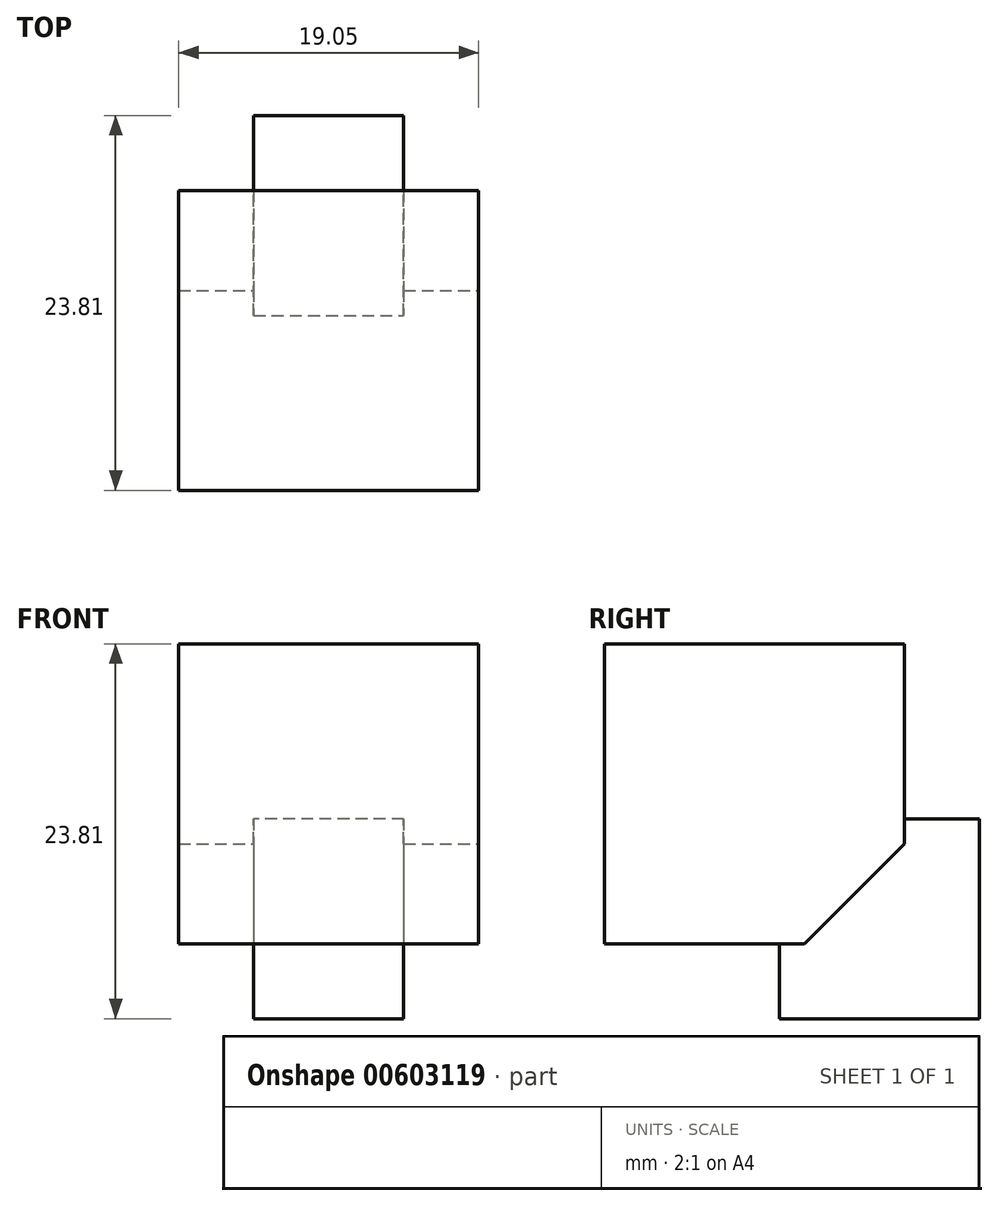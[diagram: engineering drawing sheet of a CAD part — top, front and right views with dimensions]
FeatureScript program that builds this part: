
annotation { "Feature Type Name" : "Feature", "Feature Type Description" : "" }
export const myFeature = defineFeature(function(context is Context, id is Id, definition is map)
    precondition{}
    {
        {
            var Q0;
            Q0=qCreatedBy(makeId("Front.planeOp"),FACE);
            var sketch = newSketch(context, id + "F0", { "sketchPlane" : qUnion([Q0])});
            skLineSegment(sketch, "E0.bottom", {"start": v(0, 0) * mm, "end": v(19.05, 0) * mm});
            skLineSegment(sketch, "E0.top", {"start": v(0, 19.05) * mm, "end": v(19.05, 19.05) * mm});
            skLineSegment(sketch, "E0.left", {"start": v(0, 0) * mm, "end": v(0, 19.05) * mm});
            skLineSegment(sketch, "E0.right", {"start": v(19.05, 0) * mm, "end": v(19.05, 19.05) * mm});
            skSolve(sketch);
        }
        {
            var Q0;
            Q0=qSketchRegion(id+"F0",true);
            extrude(context, id + "F1", {"entities" : qUnion([Q0]), "oppositeDirection" : true, "depth" : 19.05 * mm});
        }
        {
            var Q0;
            Q0=makeQuery(id+"F1.opExtrude","SWEPT_FACE",FACE,{"disambiguationData":[OSD([sQuery(id+"F0.wireOp",EDGE,"E0.right")])]});
            cPlane(context, id + "F2", {"entities" : qUnion([Q0]), "cplaneType" : CPlaneType.OFFSET, "offset" : 9.52 * mm, "oppositeDirection" : true, "width" : 152.4 * mm, "height" : 152.4 * mm});
        }
        {
            var Q0;
            Q0=makeQuery(id+"F1.opExtrude","SWEPT_FACE",FACE,{"disambiguationData":[OSD([sQuery(id+"F0.wireOp",EDGE,"E0.right")])]});
            var sketch = newSketch(context, id + "F3", { "sketchPlane" : qUnion([Q0])});
            skLineSegment(sketch, "E1", {"start": v(12.7, 0) * mm, "end": v(19.05, 6.35) * mm});
            skLineSegment(sketch, "E2", {"start": v(19.05, 0) * mm, "end": v(12.7, 0) * mm});
            skSolve(sketch);
        }
        {
            var Q0;
            Q0=qSketchRegion(id+"F3",true);
            var Q1;
            {var subQ0=sQuery(id+"F3.wireOp",EDGE,"E1");Q1=makeQuery(id+"F3.imprint","IMPRINT",FACE,{"disambiguationData":[TD([[makeQuery(id+"F3.imprint","IMPRINT",EDGE,{"derivedFrom":subQ0}),-1.0]])]});}
            extrude(context, id + "F4", {"entities" : qUnion([Q0, Q1]), "operationType" : NewBodyOperationType.REMOVE, "oppositeDirection" : true, "depth" : 19.05 * mm});
        }
        {
            var Q0;
            Q0=qCreatedBy(id+"F2.planeOp",FACE);
            var sketch = newSketch(context, id + "F5", { "sketchPlane" : qUnion([Q0])});
            skLineSegment(sketch, "E3.bottom", {"start": v(11.11, 7.94) * mm, "end": v(23.81, 7.94) * mm});
            skLineSegment(sketch, "E3.top", {"start": v(11.11, -4.76) * mm, "end": v(23.81, -4.76) * mm});
            skLineSegment(sketch, "E3.left", {"start": v(11.11, 7.94) * mm, "end": v(11.11, -4.76) * mm});
            skLineSegment(sketch, "E3.right", {"start": v(23.81, 7.94) * mm, "end": v(23.81, -4.76) * mm});
            skSolve(sketch);
        }
        {
            var Q0;
            Q0=qSketchRegion(id+"F5",true);
            extrude(context, id + "F6", {"entities" : qUnion([Q0]), "operationType" : NewBodyOperationType.ADD, "endBound" : BoundingType.SYMMETRIC, "depth" : 9.52 * mm, "offsetDistance" : 25.4 * mm});
        }
    });
